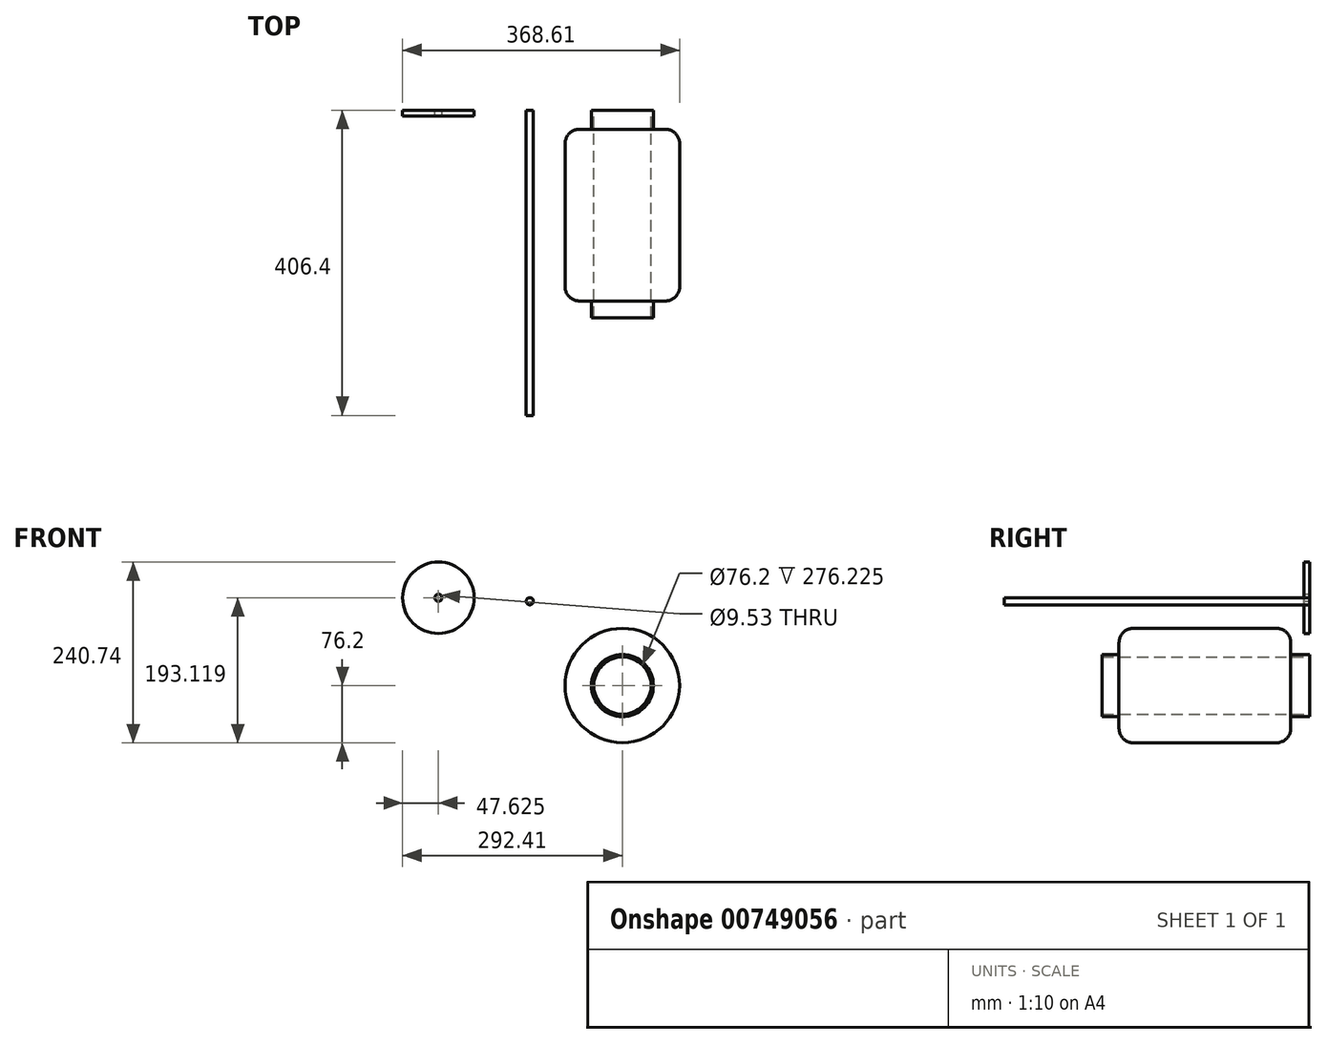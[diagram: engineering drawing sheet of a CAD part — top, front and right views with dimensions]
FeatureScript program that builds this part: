
annotation { "Feature Type Name" : "Feature", "Feature Type Description" : "" }
export const myFeature = defineFeature(function(context is Context, id is Id, definition is map)
    precondition{}
    {
        {
            var Q0;
            Q0=qCreatedBy(makeId("Front.planeOp"),FACE);
            var sketch = newSketch(context, id + "F0", { "sketchPlane" : qUnion([Q0])});
            skCircle(sketch, "E0", {"center": v(0, 0) * mm, "radius": 38.1 * mm});
            skCircle(sketch, "E1", {"center": v(0, 0) * mm, "radius": 41.28 * mm});
            skSolve(sketch);
        }
        {
            var Q0;
            Q0 = qSketchRegion(id + "F0", true);
            extrude(context, id + "F1", {"entities" : qUnion([Q0]), "depth" : 276.22 * mm, "offsetDistance" : 25.4 * mm});
        }
        {
            var Q0;
            Q0=makeQuery(id+"F1.opExtrude","CAP_FACE",FACE,{"disambiguationData":[OSD([sQuery(id+"F0.wireOp",EDGE,"E0"),sQuery(id+"F0.wireOp",EDGE,"E1")])],"isStart":true});
            var sketch = newSketch(context, id + "F2", { "sketchPlane" : qUnion([Q0])});
            skCircle(sketch, "E2", {"center": v(0, 0) * mm, "radius": 41.28 * mm});
            skCircle(sketch, "E3", {"center": v(0, 0) * mm, "radius": 76.2 * mm});
            skSolve(sketch);
        }
        {
            var Q0;
            Q0 = qSketchRegion(id + "F2", true);
            extrude(context, id + "F3", {"entities" : qUnion([Q0]), "operationType" : NewBodyOperationType.ADD, "oppositeDirection" : true, "depth" : 254 * mm, "offsetDistance" : 25.4 * mm, "hasSecondDirection" : true, "secondDirectionOppositeDirection" : true, "secondDirectionDepth" : 25.4 * mm});
        }
        {
            var Q0;
            Q0=makeQuery(id+"F3.opExtrude","CAP_EDGE",EDGE,{"disambiguationData":[OSD([sQuery(id+"F2.wireOp",EDGE,"E3")])],"isStart":true});
            var Q1;
            Q1=makeQuery(id+"F3.opExtrude","CAP_EDGE",EDGE,{"disambiguationData":[OSD([sQuery(id+"F2.wireOp",EDGE,"E3")])],"isStart":false});
            fillet(context, id + "F4", {"entities" : qUnion([Q0, Q1]), "radius" : 19.05 * mm, "tangentPropagation" : true, "allowEdgeOverflow" : false});
        }
        {
            var Q0;
            Q0=qCreatedBy(makeId("Front.planeOp"),FACE);
            var sketch = newSketch(context, id + "F5", { "sketchPlane" : qUnion([Q0])});
            skCircle(sketch, "E4", {"center": v(-244.78, 116.92) * mm, "radius": 47.63 * mm});
            skCircle(sketch, "E5", {"center": v(-244.78, 116.92) * mm, "radius": 4.76 * mm});
            skSolve(sketch);
        }
        {
            var Q0;
            Q0 = qSketchRegion(id + "F5", true);
            extrude(context, id + "F6", {"entities" : qUnion([Q0]), "depth" : 7.62 * mm, "offsetDistance" : 25.4 * mm});
        }
        {
            var Q0;
            Q0=qCreatedBy(makeId("Front.planeOp"),FACE);
            var sketch = newSketch(context, id + "F7", { "sketchPlane" : qUnion([Q0])});
            skCircle(sketch, "E6", {"center": v(-123.2, 112.26) * mm, "radius": 4.76 * mm});
            skSolve(sketch);
        }
        {
            var Q0;
            Q0 = qSketchRegion(id + "F7", true);
            extrude(context, id + "F8", {"entities" : qUnion([Q0]), "depth" : 406.4 * mm, "offsetDistance" : 25.4 * mm});
        }
    });
